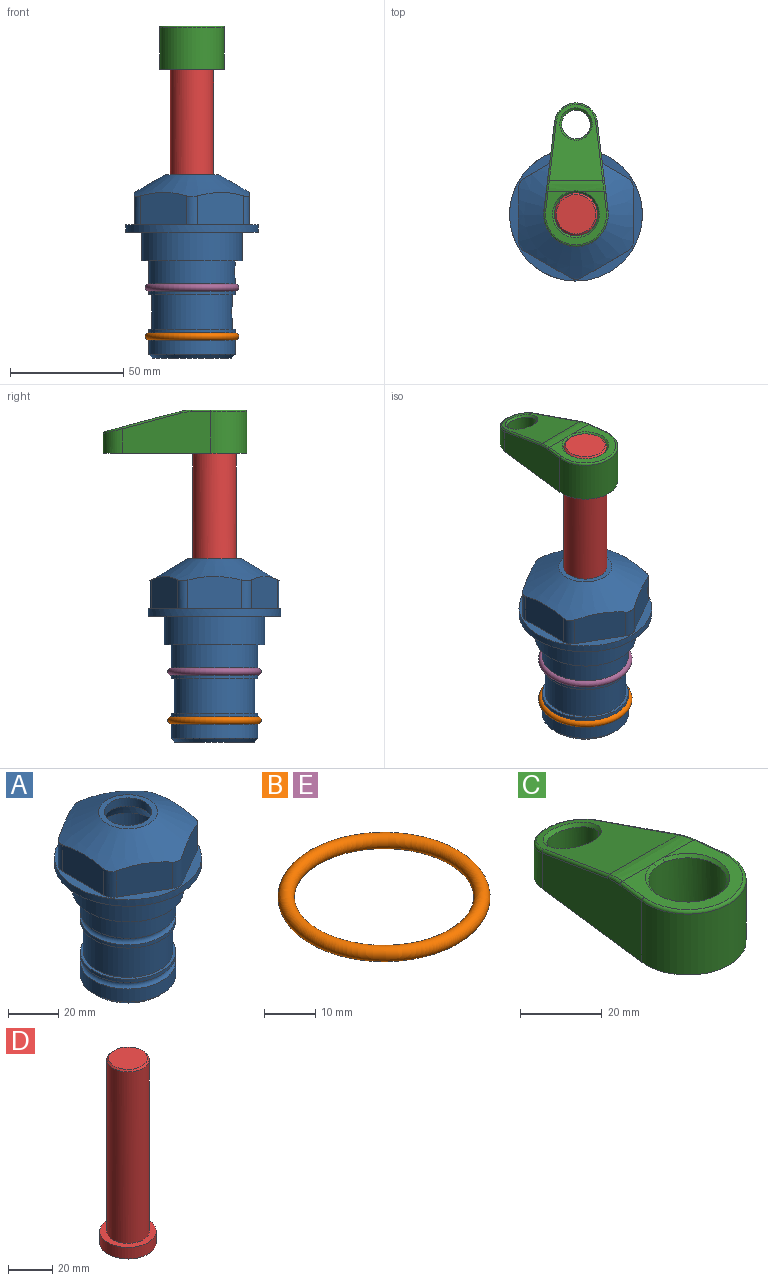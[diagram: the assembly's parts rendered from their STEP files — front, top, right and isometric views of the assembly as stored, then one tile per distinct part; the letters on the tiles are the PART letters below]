
ASSEMBLY  parts=5 mates=4
PART A: 36 faces, bbox 58.7x58.7x81 mm
  f0: cylinder r=17.78mm len=35.56mm, axis (0,0,1), area 1670.8mm2, adj f23,f24,f31
  f1: cylinder r=19.05mm len=38.1mm, axis (0,0,1), area 1191.9mm2, adj f26,f27,f30
  f2: plane 58.66x58.66mm, normal (0,0,-1), area 1150.6mm2, adj f3,f28
  f3: cylinder r=29.33mm len=58.66mm, axis (0,0,-1), area 585.1mm2, adj f2,f4
  f4: plane 58.66x58.66mm, normal (0,0,1), area 475.9mm2, adj f3,f5,f6,f7,f8,f9,f10,f11
  f5: plane 20.32x14.34mm, normal (-0.5,0.87,0), area 324.4mm2, adj f4,f15,f16,f17
  f6: plane 20.32x14.34mm, normal (0.5,0.87,0), area 324.4mm2, adj f4,f14,f15,f17
  f7: plane 23.48x14.34mm, normal (1,0,0), area 324.4mm2, adj f4,f13,f14,f17
  f8: plane 20.32x14.34mm, normal (0.5,-0.87,0), area 324.4mm2, adj f4,f12,f13,f17
  f9: plane 20.32x14.34mm, normal (-0.5,-0.87,0), area 324.4mm2, adj f4,f11,f12,f17
  f10: plane 23.48x14.34mm, normal (-1,0,0), area 324.4mm2, adj f4,f11,f16,f17
  f11: cylinder r=5.08mm len=12.85mm, axis (0,0,-1), area 67.2mm2, adj f4,f9,f10,f17
  f12: cylinder r=5.08mm len=12.85mm, axis (0,0,-1), area 67.2mm2, adj f4,f8,f9,f17
  f13: cylinder r=5.08mm len=12.85mm, axis (0,0,-1), area 67.2mm2, adj f4,f7,f8,f17
  f14: cylinder r=5.08mm len=12.85mm, axis (0,0,-1), area 67.2mm2, adj f4,f6,f7,f17
  f15: cylinder r=5.08mm len=12.85mm, axis (0,0,-1), area 67.2mm2, adj f4,f5,f6,f17
  f16: cylinder r=5.08mm len=12.85mm, axis (0,0,-1), area 67.2mm2, adj f4,f5,f10,f17
  f17: cone r=11.73mm half-angle=60deg, axis (0,0,-1), area 2071.8mm2, adj f5,f6,f7,f8,f9,f10,f11,f12
  f18: plane 23.46x23.46mm, normal (0,0,1), area 147.4mm2, adj f17,f35
  f19: plane 34.93x34.93mm, normal (0,0,-1), area 958mm2, adj f29
  f20: cylinder r=19.05mm len=38.1mm, axis (0,0,1), area 760.1mm2, adj f21,f29
  f21: torus R=19.05mm, axis (0,0,1), area 565.3mm2, adj f20,f22
  f22: cylinder r=19.05mm len=38.1mm, axis (0,0,1), area 190mm2, adj f21,f23
  f23: plane 38.1x38.1mm, normal (0,0,1), area 146.9mm2, adj f0,f22
  f24: plane 38.1x38.1mm, normal (0,0,-1), area 146.9mm2, adj f0,f25
  f25: cylinder r=19.05mm len=38.1mm, axis (0,0,1), area 190mm2, adj f24,f26
  f26: torus R=19.05mm, axis (0,0,1), area 565.3mm2, adj f1,f25
  f27: plane 44.45x44.45mm, normal (0,0,-1), area 411.7mm2, adj f1,f28
  f28: cylinder r=22.23mm len=44.45mm, axis (0,0,1), area 1773.5mm2, adj f2,f27
  f29: cone r=19.05mm half-angle=45deg, axis (0,0,1), area 257.5mm2, adj f19,f20
  f30: cylinder r=3.17mm len=6.75mm, axis (-1,0,0), area 128mm2, adj f1,f33
  f31: cylinder r=3.17mm len=6.35mm, axis (-1,0,0), area 102.5mm2, adj f0,f33
  f32: plane 25.4x25.4mm, normal (0,0,1), area 506.7mm2, adj f33
  f33: cylinder r=12.7mm len=66.42mm, axis (0,0,-1), area 5236.2mm2, adj f30,f31,f32,f34
  f34: cone r=9.53mm half-angle=30deg, axis (0,0,-1), area 443.4mm2, adj f33,f35
  f35: cylinder r=9.53mm len=19.05mm, axis (0,0,-1), area 240.9mm2, adj f18,f34
PART B: 1 faces, bbox 44.7x44.7x3.2 mm
  f0: torus R=19.05mm, axis (0,0,1), area 1193.9mm2
PART C: 31 faces, bbox 31.7x65.5x19.8 mm
  f0: plane 39.12x18.26mm, normal (0.99,0.12,0), area 612.2mm2, adj f1,f4,f7,f11,f13,f15
  f1: cylinder r=9.53mm len=18.91mm, axis (0,0,-1), area 296.1mm2, adj f0,f2,f7,f17
  f2: plane 39.12x18.26mm, normal (-0.99,0.12,0), area 612.2mm2, adj f1,f4,f7,f12,f14,f16
  f3: cylinder r=6.35mm len=12.7mm, axis (0,0,-1), area 362.4mm2, adj f7,f18
  f4: cylinder r=14.29mm len=28.58mm, axis (0,0,-1), area 882.2mm2, adj f0,f2,f7,f10
  f5: cylinder r=9.53mm len=19.05mm, axis (0,0,-1), area 1092.6mm2, adj f7,f19,f20
  f6: plane 26.99x23.69mm, normal (0,0,1), area 216.2mm2, adj f9,f10,f11,f12,f19
  f7: plane 63.5x28.58mm, normal (0,0,-1), area 661.8mm2, adj f0,f1,f2,f3,f4,f5,f22,f23
  f8: plane 33.52x23.6mm, normal (0,0.26,0.97), area 486mm2, adj f9,f15,f16,f17,f18
  f9: cylinder r=19.05mm len=24.72mm, axis (1,0,0), area 120.4mm2, adj f6,f8,f13,f14,f20
  f10: torus R=13.49mm, axis (0,0,1), area 59mm2, adj f4,f6,f11,f12
  f11: cylinder r=0.79mm len=8.67mm, axis (0.12,-0.99,0), area 10.8mm2, adj f0,f6,f10,f13
  f12: cylinder r=0.79mm len=8.67mm, axis (0.12,0.99,0), area 10.8mm2, adj f2,f6,f10,f14
  f13: bspline ~4.95x1.42mm, area 6.1mm2, adj f0,f9,f11,f15
  f14: bspline ~4.95x1.42mm, area 6.1mm2, adj f2,f9,f12,f16
  f15: cylinder r=0.79mm len=25.95mm, axis (0.12,-0.96,0.26), area 32.9mm2, adj f0,f8,f13,f17
  f16: cylinder r=0.79mm len=25.95mm, axis (0.12,0.96,-0.26), area 32.9mm2, adj f2,f8,f14,f17
  f17: bspline ~18.91x8.38mm, area 30mm2, adj f1,f8,f15,f16
  f18: bspline ~14.29x14.29mm, area 48.3mm2, adj f3,f8
  f19: cone r=9.53mm half-angle=45deg, axis (0,0,1), area 66.5mm2, adj f5,f6,f20
  f20: bspline ~3.22x0.96mm, area 3.5mm2, adj f5,f9,f19
  f21: plane 2.75x2.72mm, normal (0,0,-1), area 2.9mm2, adj f23,f25,f28
  f22: plane 23.05x15.88mm, normal (-0.99,-0.12,0), area 323.6mm2, adj f7,f25,f26,f27,f28,f29
  f23: plane 23.05x15.88mm, normal (0.99,-0.12,0), area 323.6mm2, adj f7,f21,f25,f27,f28,f30
  f24: cylinder r=9.53mm len=10.69mm, axis (0,0,-1), area 114.7mm2, adj f7,f27,f29,f30
  f25: cylinder r=12.7mm len=20.59mm, axis (0,0,-1), area 381.1mm2, adj f7,f21,f22,f23,f26,f28
  f26: plane 2.75x2.72mm, normal (0,0,-1), area 2.9mm2, adj f22,f25,f28
  f27: plane 19.72x18.37mm, normal (0,-0.26,-0.97), area 291.8mm2, adj f22,f23,f24,f28,f29,f30
  f28: cylinder r=15.88mm len=19.92mm, axis (1,0,0), area 54.8mm2, adj f21,f22,f23,f25,f26,f27
  f29: cylinder r=1.59mm len=11mm, axis (0,0,-1), area 34.7mm2, adj f7,f22,f24,f27
  f30: cylinder r=1.59mm len=11mm, axis (0,0,-1), area 34.7mm2, adj f7,f23,f24,f27
PART D: 6 faces, bbox 25.4x25.4x101.6 mm
  f0: plane 17.46x17.46mm, normal (0,0,1), area 239.5mm2, adj f5
  f1: plane 25.4x25.4mm, normal (0,0,-1), area 506.7mm2, adj f2
  f2: cylinder r=12.7mm len=25.4mm, axis (0,0,1), area 506.7mm2, adj f1,f3
  f3: plane 25.4x25.4mm, normal (0,0,1), area 221.7mm2, adj f2,f4
  f4: cylinder r=9.53mm len=94.46mm, axis (0,0,1), area 5653mm2, adj f3,f5
  f5: cone r=8.73mm half-angle=45deg, axis (0,0,-1), area 64.4mm2, adj f0,f4
PART E: same geometry as B
PLACE A at identity fixed
PLACE B t=(0,0,-21.59)mm
PLACE C rot(axis=(0.41,0.89,-0.2),0deg) t=(0,0,27.55)mm
PLACE D rot(axis=(0.41,0.89,-0.2),0deg) t=(0,0,27.55)mm
PLACE E at identity
MATE cylindrical D.f2 <-> A.f0  axis (0,0,-1) through (0,0,-10.55)mm
MATE fastened D.f2 <-> C.f4  axis (0,0,1) through (0,0,91.05)mm
MATE fastened E.f0 <-> A.f0  axis (0,0,1) through (0,0,-24.51)mm
MATE fastened B.f0 <-> A.f0  axis (0,0,1) through (0,0,-46.1)mm
